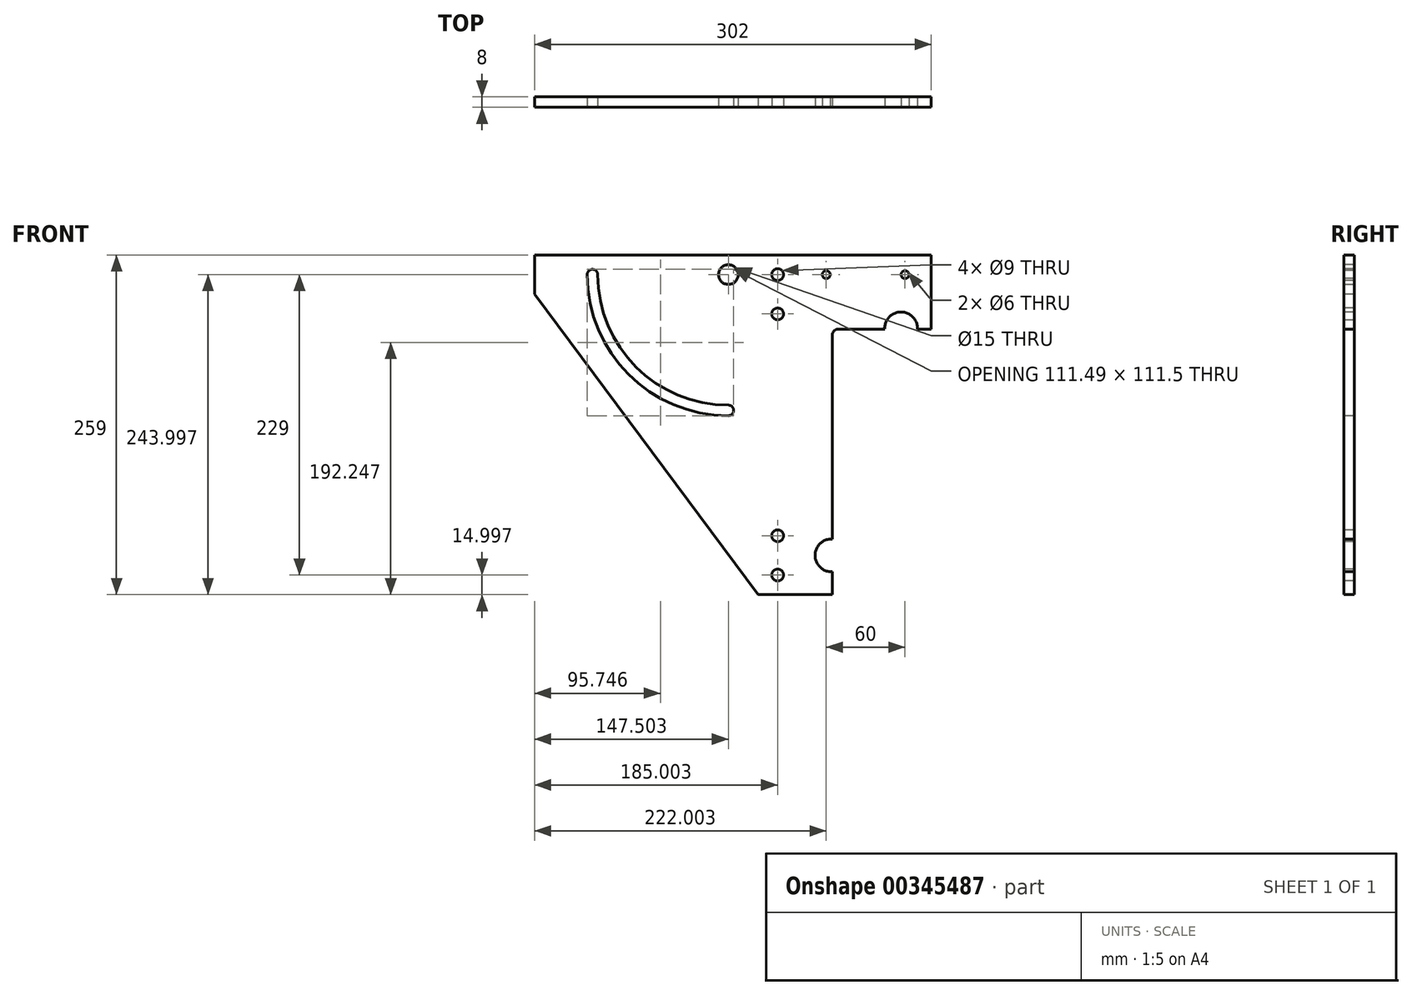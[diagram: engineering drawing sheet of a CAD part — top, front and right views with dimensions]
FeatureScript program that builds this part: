
annotation { "Feature Type Name" : "Feature", "Feature Type Description" : "" }
export const myFeature = defineFeature(function(context is Context, id is Id, definition is map)
    precondition{}
    {
        {
            var Q0;
            Q0=qCreatedBy(makeId("Front.planeOp"),FACE);
            var sketch = newSketch(context, id + "F0", { "sketchPlane" : qUnion([Q0])});
            skLineSegment(sketch, "E0.0.0", {"start": v(44.24, 117.76) * mm, "end": v(8.81, 117.76) * mm});
            skLineSegment(sketch, "E0.0.1", {"start": v(8.81, 117.76) * mm, "end": v(0.54, 111.96) * mm});
            skArc(sketch, "E0.0.2", {"start": v(0.54, 111.96) * mm, "mid": v(0.32, 111.71) * mm, "end": v(0.24, 111.4) * mm});
            skLineSegment(sketch, "E0.0.3", {"start": v(0.24, 111.4) * mm, "end": v(0.24, 96.05) * mm});
            skArc(sketch, "E0.0.4", {"start": v(0.24, 96.05) * mm, "mid": v(0.3, 95.78) * mm, "end": v(0.45, 95.55) * mm});
            skLineSegment(sketch, "E0.0.5", {"start": v(0.45, 95.55) * mm, "end": v(4.54, 91.46) * mm});
            skArc(sketch, "E0.0.6", {"start": v(4.54, 91.46) * mm, "mid": v(4.76, 91.31) * mm, "end": v(5.03, 91.26) * mm});
            skLineSegment(sketch, "E0.0.7", {"start": v(5.03, 91.26) * mm, "end": v(11.74, 91.26) * mm});
            skArc(sketch, "E0.0.8", {"start": v(11.74, 91.26) * mm, "mid": v(12.1, 91.4) * mm, "end": v(12.24, 91.76) * mm});
            skArc(sketch, "E0.0.9", {"start": v(12.24, 91.76) * mm, "mid": v(27.6, 98.12) * mm, "end": v(21.24, 82.76) * mm});
            skArc(sketch, "E0.0.10", {"start": v(21.24, 82.76) * mm, "mid": v(20.89, 82.61) * mm, "end": v(20.74, 82.26) * mm});
            skLineSegment(sketch, "E0.0.11", {"start": v(20.74, 82.26) * mm, "end": v(20.74, 81.05) * mm});
            skArc(sketch, "E0.0.12", {"start": v(20.74, 81.05) * mm, "mid": v(20.8, 80.78) * mm, "end": v(20.95, 80.55) * mm});
            skLineSegment(sketch, "E0.0.13", {"start": v(20.95, 80.55) * mm, "end": v(22.04, 79.46) * mm});
            skArc(sketch, "E0.0.14", {"start": v(22.04, 79.46) * mm, "mid": v(22.26, 79.31) * mm, "end": v(22.53, 79.26) * mm});
            skLineSegment(sketch, "E0.0.15", {"start": v(22.53, 79.26) * mm, "end": v(31.95, 79.26) * mm});
            skArc(sketch, "E0.0.16", {"start": v(31.95, 79.26) * mm, "mid": v(32.22, 79.31) * mm, "end": v(32.45, 79.46) * mm});
            skLineSegment(sketch, "E0.0.17", {"start": v(32.45, 79.46) * mm, "end": v(44.04, 91.05) * mm});
            skArc(sketch, "E0.0.18", {"start": v(44.04, 91.05) * mm, "mid": v(44.19, 91.28) * mm, "end": v(44.24, 91.55) * mm});
            skLineSegment(sketch, "E0.0.19", {"start": v(44.24, 91.55) * mm, "end": v(44.24, 117.76) * mm});
            skLineSegment(sketch, "E1.0.0", {"start": v(-3.56, 77.96) * mm, "end": v(8.04, 77.96) * mm});
            skLineSegment(sketch, "E1.0.1", {"start": v(8.04, 77.96) * mm, "end": v(8.24, 77.76) * mm});
            skLineSegment(sketch, "E1.0.2", {"start": v(18.24, 77.76) * mm, "end": v(8.24, 77.76) * mm});
            skLineSegment(sketch, "E1.0.3", {"start": v(18.24, 77.76) * mm, "end": v(18.74, 77.76) * mm});
            skLineSegment(sketch, "E1.0.4", {"start": v(18.74, 77.76) * mm, "end": v(19.24, 78.26) * mm});
            skLineSegment(sketch, "E1.0.5", {"start": v(19.24, 78.26) * mm, "end": v(19.24, 82.27) * mm});
            skArc(sketch, "E1.0.6", {"start": v(19.24, 82.27) * mm, "mid": v(19.71, 83.36) * mm, "end": v(20.82, 83.77) * mm});
            skArc(sketch, "E1.0.7", {"start": v(20.82, 83.77) * mm, "mid": v(26.72, 97.6) * mm, "end": v(13.3, 90.83) * mm});
            skArc(sketch, "E1.0.8", {"start": v(13.3, 90.83) * mm, "mid": v(13.3, 90.56) * mm, "end": v(13.2, 90.3) * mm});
            skLineSegment(sketch, "E1.0.9", {"start": v(13.2, 90.3) * mm, "end": v(11.09, 85.74) * mm});
            skArc(sketch, "E1.0.10", {"start": v(11.09, 85.74) * mm, "mid": v(10.72, 85.39) * mm, "end": v(10.23, 85.26) * mm});
            skLineSegment(sketch, "E1.0.11", {"start": v(10.23, 85.26) * mm, "end": v(2.74, 85.26) * mm});
            skLineSegment(sketch, "E1.0.12", {"start": v(2.74, 85.26) * mm, "end": v(2.24, 84.97) * mm});
            skLineSegment(sketch, "E1.0.13", {"start": v(2.24, 84.97) * mm, "end": v(1.74, 85.26) * mm});
            skLineSegment(sketch, "E1.0.14", {"start": v(1.74, 85.26) * mm, "end": v(-7.36, 85.26) * mm});
            skLineSegment(sketch, "E1.0.15", {"start": v(-7.36, 85.26) * mm, "end": v(-7.76, 84.86) * mm});
            skLineSegment(sketch, "E1.0.16", {"start": v(-7.76, 84.86) * mm, "end": v(-7.76, 78.16) * mm});
            skLineSegment(sketch, "E1.0.17", {"start": v(-7.76, 78.16) * mm, "end": v(-7.36, 77.76) * mm});
            skLineSegment(sketch, "E1.0.18", {"start": v(-3.76, 77.76) * mm, "end": v(-7.36, 77.76) * mm});
            skLineSegment(sketch, "E1.0.19", {"start": v(-3.76, 77.76) * mm, "end": v(-3.56, 77.96) * mm});
            skArc(sketch, "E2.0.0", {"start": v(-13.76, -69.24) * mm, "mid": v(-13.4, -69.1) * mm, "end": v(-13.26, -68.74) * mm});
            skLineSegment(sketch, "E2.0.1", {"start": v(-13.26, -68.74) * mm, "end": v(-13.26, -67.24) * mm});
            skArc(sketch, "E2.0.2", {"start": v(-13.26, -67.24) * mm, "mid": v(-13.55, -66.54) * mm, "end": v(-14.26, -66.24) * mm});
            skLineSegment(sketch, "E2.0.3", {"start": v(-14.26, -66.24) * mm, "end": v(-16.26, -66.24) * mm});
            skArc(sketch, "E2.0.4", {"start": v(-16.26, -66.24) * mm, "mid": v(-17.32, -66.68) * mm, "end": v(-17.76, -67.74) * mm});
            skLineSegment(sketch, "E2.0.5", {"start": v(-17.76, -67.74) * mm, "end": v(-17.76, -68.24) * mm});
            skLineSegment(sketch, "E2.0.6", {"start": v(-17.76, -68.24) * mm, "end": v(-17.76, -78.24) * mm});
            skArc(sketch, "E2.0.7", {"start": v(-17.76, -78.24) * mm, "mid": v(-16.59, -81.07) * mm, "end": v(-13.76, -82.24) * mm});
            skLineSegment(sketch, "E2.0.8", {"start": v(-13.76, -82.24) * mm, "end": v(-3.26, -82.24) * mm});
            skArc(sketch, "E2.0.9", {"start": v(-3.26, -82.24) * mm, "mid": v(-2.2, -81.8) * mm, "end": v(-1.76, -80.74) * mm});
            skLineSegment(sketch, "E2.0.10", {"start": v(-1.76, -80.74) * mm, "end": v(-1.76, -78.74) * mm});
            skArc(sketch, "E2.0.11", {"start": v(-1.76, -78.74) * mm, "mid": v(-2.05, -78.04) * mm, "end": v(-2.76, -77.74) * mm});
            skLineSegment(sketch, "E2.0.12", {"start": v(-2.76, -77.74) * mm, "end": v(-4.26, -77.74) * mm});
            skArc(sketch, "E2.0.13", {"start": v(-4.26, -77.74) * mm, "mid": v(-4.61, -77.89) * mm, "end": v(-4.76, -78.24) * mm});
            skLineSegment(sketch, "E2.0.14", {"start": v(-4.76, -78.24) * mm, "end": v(-4.76, -79.8) * mm});
            skArc(sketch, "E2.0.15", {"start": v(-4.76, -79.8) * mm, "mid": v(-4.89, -80.11) * mm, "end": v(-5.2, -80.24) * mm});
            skLineSegment(sketch, "E2.0.16", {"start": v(-5.2, -80.24) * mm, "end": v(-5.26, -80.24) * mm});
            skArc(sketch, "E2.0.17", {"start": v(-5.26, -80.24) * mm, "mid": v(-7.03, -79.51) * mm, "end": v(-7.76, -77.74) * mm});
            skLineSegment(sketch, "E2.0.18", {"start": v(-7.76, -77.74) * mm, "end": v(-7.76, -76.44) * mm});
            skArc(sketch, "E2.0.19", {"start": v(-7.76, -76.44) * mm, "mid": v(-7.38, -74.52) * mm, "end": v(-6.3, -72.9) * mm});
            skLineSegment(sketch, "E2.0.20", {"start": v(-6.3, -72.9) * mm, "end": v(-4.85, -71.46) * mm});
            skArc(sketch, "E2.0.21", {"start": v(-4.85, -71.46) * mm, "mid": v(-3.23, -70.37) * mm, "end": v(-1.31, -70) * mm});
            skLineSegment(sketch, "E2.0.22", {"start": v(-1.31, -70) * mm, "end": v(5.8, -70) * mm});
            skArc(sketch, "E2.0.23", {"start": v(5.8, -70) * mm, "mid": v(7.71, -70.37) * mm, "end": v(9.34, -71.46) * mm});
            skLineSegment(sketch, "E2.0.24", {"start": v(9.34, -71.46) * mm, "end": v(10.78, -72.9) * mm});
            skArc(sketch, "E2.0.25", {"start": v(10.78, -72.9) * mm, "mid": v(11.86, -74.52) * mm, "end": v(12.24, -76.44) * mm});
            skLineSegment(sketch, "E2.0.26", {"start": v(12.24, -76.44) * mm, "end": v(12.24, -77.74) * mm});
            skArc(sketch, "E2.0.27", {"start": v(12.24, -77.74) * mm, "mid": v(11.51, -79.51) * mm, "end": v(9.74, -80.24) * mm});
            skLineSegment(sketch, "E2.0.28", {"start": v(9.74, -80.24) * mm, "end": v(9.7, -80.24) * mm});
            skArc(sketch, "E2.0.29", {"start": v(9.7, -80.24) * mm, "mid": v(9.37, -80.11) * mm, "end": v(9.24, -79.8) * mm});
            skLineSegment(sketch, "E2.0.30", {"start": v(9.24, -79.8) * mm, "end": v(9.24, -78.24) * mm});
            skArc(sketch, "E2.0.31", {"start": v(9.24, -78.24) * mm, "mid": v(9.1, -77.89) * mm, "end": v(8.74, -77.74) * mm});
            skLineSegment(sketch, "E2.0.32", {"start": v(8.74, -77.74) * mm, "end": v(7.24, -77.74) * mm});
            skArc(sketch, "E2.0.33", {"start": v(7.24, -77.74) * mm, "mid": v(6.54, -78.04) * mm, "end": v(6.24, -78.74) * mm});
            skLineSegment(sketch, "E2.0.34", {"start": v(6.24, -78.74) * mm, "end": v(6.24, -80.74) * mm});
            skArc(sketch, "E2.0.35", {"start": v(6.24, -80.74) * mm, "mid": v(6.68, -81.8) * mm, "end": v(7.74, -82.24) * mm});
            skLineSegment(sketch, "E2.0.36", {"start": v(7.74, -82.24) * mm, "end": v(18.24, -82.24) * mm});
            skArc(sketch, "E2.0.37", {"start": v(18.24, -82.24) * mm, "mid": v(21.07, -81.07) * mm, "end": v(22.24, -78.24) * mm});
            skLineSegment(sketch, "E2.0.38", {"start": v(22.24, -78.24) * mm, "end": v(22.24, -67.74) * mm});
            skArc(sketch, "E2.0.39", {"start": v(22.24, -67.74) * mm, "mid": v(21.8, -66.68) * mm, "end": v(20.74, -66.24) * mm});
            skLineSegment(sketch, "E2.0.40", {"start": v(20.74, -66.24) * mm, "end": v(18.74, -66.24) * mm});
            skArc(sketch, "E2.0.41", {"start": v(18.74, -66.24) * mm, "mid": v(18.04, -66.54) * mm, "end": v(17.74, -67.24) * mm});
            skLineSegment(sketch, "E2.0.42", {"start": v(17.74, -67.24) * mm, "end": v(17.74, -68.74) * mm});
            skArc(sketch, "E2.0.43", {"start": v(17.74, -68.74) * mm, "mid": v(17.89, -69.1) * mm, "end": v(18.24, -69.24) * mm});
            skLineSegment(sketch, "E2.0.44", {"start": v(18.24, -69.24) * mm, "end": v(19.8, -69.24) * mm});
            skArc(sketch, "E2.0.45", {"start": v(19.8, -69.24) * mm, "mid": v(20.11, -69.37) * mm, "end": v(20.24, -69.7) * mm});
            skLineSegment(sketch, "E2.0.46", {"start": v(20.24, -69.7) * mm, "end": v(20.24, -69.74) * mm});
            skArc(sketch, "E2.0.47", {"start": v(20.24, -69.74) * mm, "mid": v(19.51, -71.51) * mm, "end": v(17.74, -72.24) * mm});
            skLineSegment(sketch, "E2.0.48", {"start": v(17.74, -72.24) * mm, "end": v(16.44, -72.24) * mm});
            skArc(sketch, "E2.0.49", {"start": v(16.44, -72.24) * mm, "mid": v(14.52, -71.86) * mm, "end": v(12.9, -70.78) * mm});
            skLineSegment(sketch, "E2.0.50", {"start": v(12.9, -70.78) * mm, "end": v(11.46, -69.34) * mm});
            skArc(sketch, "E2.0.51", {"start": v(11.46, -69.34) * mm, "mid": v(10.37, -67.71) * mm, "end": v(10, -65.8) * mm});
            skLineSegment(sketch, "E2.0.52", {"start": v(10, -65.8) * mm, "end": v(10, -58.69) * mm});
            skArc(sketch, "E2.0.53", {"start": v(10, -58.69) * mm, "mid": v(10.37, -56.77) * mm, "end": v(11.46, -55.15) * mm});
            skLineSegment(sketch, "E2.0.54", {"start": v(11.46, -55.15) * mm, "end": v(12.9, -53.7) * mm});
            skArc(sketch, "E2.0.55", {"start": v(12.9, -53.7) * mm, "mid": v(14.52, -52.62) * mm, "end": v(16.44, -52.24) * mm});
            skLineSegment(sketch, "E2.0.56", {"start": v(16.44, -52.24) * mm, "end": v(17.74, -52.24) * mm});
            skArc(sketch, "E2.0.57", {"start": v(17.74, -52.24) * mm, "mid": v(19.51, -52.97) * mm, "end": v(20.24, -54.74) * mm});
            skLineSegment(sketch, "E2.0.58", {"start": v(20.24, -54.74) * mm, "end": v(20.24, -54.8) * mm});
            skArc(sketch, "E2.0.59", {"start": v(20.24, -54.8) * mm, "mid": v(20.11, -55.11) * mm, "end": v(19.8, -55.24) * mm});
            skLineSegment(sketch, "E2.0.60", {"start": v(19.8, -55.24) * mm, "end": v(18.24, -55.24) * mm});
            skArc(sketch, "E2.0.61", {"start": v(18.24, -55.24) * mm, "mid": v(17.89, -55.39) * mm, "end": v(17.74, -55.74) * mm});
            skLineSegment(sketch, "E2.0.62", {"start": v(17.74, -55.74) * mm, "end": v(17.74, -57.24) * mm});
            skArc(sketch, "E2.0.63", {"start": v(17.74, -57.24) * mm, "mid": v(18.04, -57.95) * mm, "end": v(18.74, -58.24) * mm});
            skLineSegment(sketch, "E2.0.64", {"start": v(18.74, -58.24) * mm, "end": v(20.74, -58.24) * mm});
            skArc(sketch, "E2.0.65", {"start": v(20.74, -58.24) * mm, "mid": v(21.8, -57.8) * mm, "end": v(22.24, -56.74) * mm});
            skLineSegment(sketch, "E2.0.66", {"start": v(22.24, -56.74) * mm, "end": v(22.24, -27.74) * mm});
            skArc(sketch, "E2.0.67", {"start": v(22.24, -27.74) * mm, "mid": v(21.8, -26.68) * mm, "end": v(20.74, -26.24) * mm});
            skLineSegment(sketch, "E2.0.68", {"start": v(20.74, -26.24) * mm, "end": v(18.74, -26.24) * mm});
            skArc(sketch, "E2.0.69", {"start": v(18.74, -26.24) * mm, "mid": v(18.04, -26.54) * mm, "end": v(17.74, -27.24) * mm});
            skLineSegment(sketch, "E2.0.70", {"start": v(17.74, -27.24) * mm, "end": v(17.74, -28.74) * mm});
            skArc(sketch, "E2.0.71", {"start": v(17.74, -28.74) * mm, "mid": v(17.89, -29.1) * mm, "end": v(18.24, -29.24) * mm});
            skLineSegment(sketch, "E2.0.72", {"start": v(18.24, -29.24) * mm, "end": v(19.8, -29.24) * mm});
            skArc(sketch, "E2.0.73", {"start": v(19.8, -29.24) * mm, "mid": v(20.11, -29.37) * mm, "end": v(20.24, -29.7) * mm});
            skLineSegment(sketch, "E2.0.74", {"start": v(20.24, -29.7) * mm, "end": v(20.24, -29.74) * mm});
            skArc(sketch, "E2.0.75", {"start": v(20.24, -29.74) * mm, "mid": v(19.51, -31.51) * mm, "end": v(17.74, -32.24) * mm});
            skLineSegment(sketch, "E2.0.76", {"start": v(17.74, -32.24) * mm, "end": v(16.44, -32.24) * mm});
            skArc(sketch, "E2.0.77", {"start": v(16.44, -32.24) * mm, "mid": v(14.52, -31.86) * mm, "end": v(12.9, -30.78) * mm});
            skLineSegment(sketch, "E2.0.78", {"start": v(12.9, -30.78) * mm, "end": v(11.46, -29.34) * mm});
            skArc(sketch, "E2.0.79", {"start": v(11.46, -29.34) * mm, "mid": v(10.37, -27.71) * mm, "end": v(10, -25.8) * mm});
            skLineSegment(sketch, "E2.0.80", {"start": v(10, -25.8) * mm, "end": v(10, -18.69) * mm});
            skArc(sketch, "E2.0.81", {"start": v(10, -18.69) * mm, "mid": v(10.37, -16.77) * mm, "end": v(11.46, -15.15) * mm});
            skLineSegment(sketch, "E2.0.82", {"start": v(11.46, -15.15) * mm, "end": v(12.9, -13.7) * mm});
            skArc(sketch, "E2.0.83", {"start": v(12.9, -13.7) * mm, "mid": v(14.52, -12.62) * mm, "end": v(16.44, -12.24) * mm});
            skLineSegment(sketch, "E2.0.84", {"start": v(16.44, -12.24) * mm, "end": v(17.74, -12.24) * mm});
            skArc(sketch, "E2.0.85", {"start": v(17.74, -12.24) * mm, "mid": v(19.51, -12.97) * mm, "end": v(20.24, -14.74) * mm});
            skLineSegment(sketch, "E2.0.86", {"start": v(20.24, -14.74) * mm, "end": v(20.24, -14.8) * mm});
            skArc(sketch, "E2.0.87", {"start": v(20.24, -14.8) * mm, "mid": v(20.11, -15.11) * mm, "end": v(19.8, -15.24) * mm});
            skLineSegment(sketch, "E2.0.88", {"start": v(19.8, -15.24) * mm, "end": v(18.24, -15.24) * mm});
            skArc(sketch, "E2.0.89", {"start": v(18.24, -15.24) * mm, "mid": v(17.89, -15.39) * mm, "end": v(17.74, -15.74) * mm});
            skLineSegment(sketch, "E2.0.90", {"start": v(17.74, -15.74) * mm, "end": v(17.74, -17.24) * mm});
            skArc(sketch, "E2.0.91", {"start": v(17.74, -17.24) * mm, "mid": v(18.04, -17.95) * mm, "end": v(18.74, -18.24) * mm});
            skLineSegment(sketch, "E2.0.92", {"start": v(18.74, -18.24) * mm, "end": v(20.74, -18.24) * mm});
            skArc(sketch, "E2.0.93", {"start": v(20.74, -18.24) * mm, "mid": v(21.8, -17.8) * mm, "end": v(22.24, -16.74) * mm});
            skLineSegment(sketch, "E2.0.94", {"start": v(22.24, -16.74) * mm, "end": v(22.24, 12.26) * mm});
            skArc(sketch, "E2.0.95", {"start": v(22.24, 12.26) * mm, "mid": v(21.8, 13.32) * mm, "end": v(20.74, 13.76) * mm});
            skLineSegment(sketch, "E2.0.96", {"start": v(20.74, 13.76) * mm, "end": v(18.74, 13.76) * mm});
            skArc(sketch, "E2.0.97", {"start": v(18.74, 13.76) * mm, "mid": v(18.04, 13.46) * mm, "end": v(17.74, 12.76) * mm});
            skLineSegment(sketch, "E2.0.98", {"start": v(17.74, 12.76) * mm, "end": v(17.74, 11.26) * mm});
            skArc(sketch, "E2.0.99", {"start": v(17.74, 11.26) * mm, "mid": v(17.89, 10.9) * mm, "end": v(18.24, 10.76) * mm});
            skLineSegment(sketch, "E2.0.100", {"start": v(18.24, 10.76) * mm, "end": v(19.8, 10.76) * mm});
            skArc(sketch, "E2.0.101", {"start": v(19.8, 10.76) * mm, "mid": v(20.11, 10.63) * mm, "end": v(20.24, 10.3) * mm});
            skLineSegment(sketch, "E2.0.102", {"start": v(20.24, 10.3) * mm, "end": v(20.24, 10.26) * mm});
            skArc(sketch, "E2.0.103", {"start": v(20.24, 10.26) * mm, "mid": v(19.51, 8.49) * mm, "end": v(17.74, 7.76) * mm});
            skLineSegment(sketch, "E2.0.104", {"start": v(17.74, 7.76) * mm, "end": v(16.44, 7.76) * mm});
            skArc(sketch, "E2.0.105", {"start": v(16.44, 7.76) * mm, "mid": v(14.52, 8.14) * mm, "end": v(12.9, 9.22) * mm});
            skLineSegment(sketch, "E2.0.106", {"start": v(12.9, 9.22) * mm, "end": v(11.46, 10.66) * mm});
            skArc(sketch, "E2.0.107", {"start": v(11.46, 10.66) * mm, "mid": v(10.37, 12.29) * mm, "end": v(10, 14.2) * mm});
            skLineSegment(sketch, "E2.0.108", {"start": v(10, 14.2) * mm, "end": v(10, 21.31) * mm});
            skArc(sketch, "E2.0.109", {"start": v(10, 21.31) * mm, "mid": v(10.37, 23.23) * mm, "end": v(11.46, 24.85) * mm});
            skLineSegment(sketch, "E2.0.110", {"start": v(11.46, 24.85) * mm, "end": v(12.9, 26.3) * mm});
            skArc(sketch, "E2.0.111", {"start": v(12.9, 26.3) * mm, "mid": v(14.52, 27.38) * mm, "end": v(16.44, 27.76) * mm});
            skLineSegment(sketch, "E2.0.112", {"start": v(16.44, 27.76) * mm, "end": v(17.74, 27.76) * mm});
            skArc(sketch, "E2.0.113", {"start": v(17.74, 27.76) * mm, "mid": v(19.51, 27.03) * mm, "end": v(20.24, 25.26) * mm});
            skLineSegment(sketch, "E2.0.114", {"start": v(20.24, 25.26) * mm, "end": v(20.24, 25.2) * mm});
            skArc(sketch, "E2.0.115", {"start": v(20.24, 25.2) * mm, "mid": v(20.11, 24.89) * mm, "end": v(19.8, 24.76) * mm});
            skLineSegment(sketch, "E2.0.116", {"start": v(19.8, 24.76) * mm, "end": v(18.24, 24.76) * mm});
            skArc(sketch, "E2.0.117", {"start": v(18.24, 24.76) * mm, "mid": v(17.89, 24.61) * mm, "end": v(17.74, 24.26) * mm});
            skLineSegment(sketch, "E2.0.118", {"start": v(17.74, 24.26) * mm, "end": v(17.74, 22.76) * mm});
            skArc(sketch, "E2.0.119", {"start": v(17.74, 22.76) * mm, "mid": v(18.04, 22.05) * mm, "end": v(18.74, 21.76) * mm});
            skLineSegment(sketch, "E2.0.120", {"start": v(18.74, 21.76) * mm, "end": v(20.74, 21.76) * mm});
            skArc(sketch, "E2.0.121", {"start": v(20.74, 21.76) * mm, "mid": v(21.8, 22.2) * mm, "end": v(22.24, 23.26) * mm});
            skLineSegment(sketch, "E2.0.122", {"start": v(22.24, 23.26) * mm, "end": v(22.24, 52.26) * mm});
            skArc(sketch, "E2.0.123", {"start": v(22.24, 52.26) * mm, "mid": v(21.8, 53.32) * mm, "end": v(20.74, 53.76) * mm});
            skLineSegment(sketch, "E2.0.124", {"start": v(20.74, 53.76) * mm, "end": v(18.74, 53.76) * mm});
            skArc(sketch, "E2.0.125", {"start": v(18.74, 53.76) * mm, "mid": v(18.04, 53.46) * mm, "end": v(17.74, 52.76) * mm});
            skLineSegment(sketch, "E2.0.126", {"start": v(17.74, 52.76) * mm, "end": v(17.74, 51.26) * mm});
            skArc(sketch, "E2.0.127", {"start": v(17.74, 51.26) * mm, "mid": v(17.89, 50.9) * mm, "end": v(18.24, 50.76) * mm});
            skLineSegment(sketch, "E2.0.128", {"start": v(18.24, 50.76) * mm, "end": v(19.8, 50.76) * mm});
            skArc(sketch, "E2.0.129", {"start": v(19.8, 50.76) * mm, "mid": v(20.11, 50.63) * mm, "end": v(20.24, 50.3) * mm});
            skLineSegment(sketch, "E2.0.130", {"start": v(20.24, 50.3) * mm, "end": v(20.24, 50.26) * mm});
            skArc(sketch, "E2.0.131", {"start": v(20.24, 50.26) * mm, "mid": v(19.51, 48.49) * mm, "end": v(17.74, 47.76) * mm});
            skLineSegment(sketch, "E2.0.132", {"start": v(17.74, 47.76) * mm, "end": v(16.44, 47.76) * mm});
            skArc(sketch, "E2.0.133", {"start": v(16.44, 47.76) * mm, "mid": v(14.52, 48.14) * mm, "end": v(12.9, 49.22) * mm});
            skLineSegment(sketch, "E2.0.134", {"start": v(12.9, 49.22) * mm, "end": v(11.46, 50.66) * mm});
            skArc(sketch, "E2.0.135", {"start": v(11.46, 50.66) * mm, "mid": v(10.37, 52.29) * mm, "end": v(10, 54.2) * mm});
            skLineSegment(sketch, "E2.0.136", {"start": v(10, 54.2) * mm, "end": v(10, 61.31) * mm});
            skArc(sketch, "E2.0.137", {"start": v(10, 61.31) * mm, "mid": v(10.37, 63.23) * mm, "end": v(11.46, 64.85) * mm});
            skLineSegment(sketch, "E2.0.138", {"start": v(11.46, 64.85) * mm, "end": v(12.9, 66.3) * mm});
            skArc(sketch, "E2.0.139", {"start": v(12.9, 66.3) * mm, "mid": v(14.52, 67.38) * mm, "end": v(16.44, 67.76) * mm});
            skLineSegment(sketch, "E2.0.140", {"start": v(16.44, 67.76) * mm, "end": v(17.74, 67.76) * mm});
            skArc(sketch, "E2.0.141", {"start": v(17.74, 67.76) * mm, "mid": v(19.51, 67.03) * mm, "end": v(20.24, 65.26) * mm});
            skLineSegment(sketch, "E2.0.142", {"start": v(20.24, 65.26) * mm, "end": v(20.24, 65.2) * mm});
            skArc(sketch, "E2.0.143", {"start": v(20.24, 65.2) * mm, "mid": v(20.11, 64.89) * mm, "end": v(19.8, 64.76) * mm});
            skLineSegment(sketch, "E2.0.144", {"start": v(19.8, 64.76) * mm, "end": v(18.24, 64.76) * mm});
            skArc(sketch, "E2.0.145", {"start": v(18.24, 64.76) * mm, "mid": v(17.89, 64.61) * mm, "end": v(17.74, 64.26) * mm});
            skLineSegment(sketch, "E2.0.146", {"start": v(17.74, 64.26) * mm, "end": v(17.74, 62.76) * mm});
            skArc(sketch, "E2.0.147", {"start": v(17.74, 62.76) * mm, "mid": v(18.04, 62.05) * mm, "end": v(18.74, 61.76) * mm});
            skLineSegment(sketch, "E2.0.148", {"start": v(18.74, 61.76) * mm, "end": v(20.74, 61.76) * mm});
            skArc(sketch, "E2.0.149", {"start": v(20.74, 61.76) * mm, "mid": v(21.8, 62.2) * mm, "end": v(22.24, 63.26) * mm});
            skLineSegment(sketch, "E2.0.150", {"start": v(22.24, 63.26) * mm, "end": v(22.24, 73.76) * mm});
            skArc(sketch, "E2.0.151", {"start": v(22.24, 73.76) * mm, "mid": v(21.07, 76.59) * mm, "end": v(18.24, 77.76) * mm});
            skLineSegment(sketch, "E2.0.153", {"start": v(8.24, 77.76) * mm, "end": v(7.74, 77.76) * mm});
            skArc(sketch, "E2.0.154", {"start": v(7.74, 77.76) * mm, "mid": v(6.68, 77.32) * mm, "end": v(6.24, 76.26) * mm});
            skLineSegment(sketch, "E2.0.155", {"start": v(6.24, 76.26) * mm, "end": v(6.24, 74.26) * mm});
            skArc(sketch, "E2.0.156", {"start": v(6.24, 74.26) * mm, "mid": v(6.54, 73.55) * mm, "end": v(7.24, 73.26) * mm});
            skLineSegment(sketch, "E2.0.157", {"start": v(7.24, 73.26) * mm, "end": v(8.74, 73.26) * mm});
            skArc(sketch, "E2.0.158", {"start": v(8.74, 73.26) * mm, "mid": v(9.1, 73.4) * mm, "end": v(9.24, 73.76) * mm});
            skLineSegment(sketch, "E2.0.159", {"start": v(9.24, 73.76) * mm, "end": v(9.24, 75.3) * mm});
            skArc(sketch, "E2.0.160", {"start": v(9.24, 75.3) * mm, "mid": v(9.37, 75.63) * mm, "end": v(9.7, 75.76) * mm});
            skLineSegment(sketch, "E2.0.161", {"start": v(9.7, 75.76) * mm, "end": v(9.74, 75.76) * mm});
            skArc(sketch, "E2.0.162", {"start": v(9.74, 75.76) * mm, "mid": v(11.51, 75.03) * mm, "end": v(12.24, 73.26) * mm});
            skLineSegment(sketch, "E2.0.163", {"start": v(12.24, 73.26) * mm, "end": v(12.24, 71.95) * mm});
            skArc(sketch, "E2.0.164", {"start": v(12.24, 71.95) * mm, "mid": v(11.86, 70.04) * mm, "end": v(10.78, 68.41) * mm});
            skLineSegment(sketch, "E2.0.165", {"start": v(10.78, 68.41) * mm, "end": v(9.34, 66.97) * mm});
            skArc(sketch, "E2.0.166", {"start": v(9.34, 66.97) * mm, "mid": v(7.71, 65.89) * mm, "end": v(5.8, 65.5) * mm});
            skLineSegment(sketch, "E2.0.167", {"start": v(5.8, 65.5) * mm, "end": v(-1.31, 65.5) * mm});
            skArc(sketch, "E2.0.168", {"start": v(-1.31, 65.5) * mm, "mid": v(-3.23, 65.89) * mm, "end": v(-4.85, 66.97) * mm});
            skLineSegment(sketch, "E2.0.169", {"start": v(-4.85, 66.97) * mm, "end": v(-6.3, 68.41) * mm});
            skArc(sketch, "E2.0.170", {"start": v(-6.3, 68.41) * mm, "mid": v(-7.38, 70.04) * mm, "end": v(-7.76, 71.95) * mm});
            skLineSegment(sketch, "E2.0.171", {"start": v(-7.76, 71.95) * mm, "end": v(-7.76, 73.26) * mm});
            skArc(sketch, "E2.0.172", {"start": v(-7.76, 73.26) * mm, "mid": v(-7.03, 75.03) * mm, "end": v(-5.26, 75.76) * mm});
            skLineSegment(sketch, "E2.0.173", {"start": v(-5.26, 75.76) * mm, "end": v(-5.2, 75.76) * mm});
            skArc(sketch, "E2.0.174", {"start": v(-5.2, 75.76) * mm, "mid": v(-4.89, 75.63) * mm, "end": v(-4.76, 75.3) * mm});
            skLineSegment(sketch, "E2.0.175", {"start": v(-4.76, 75.3) * mm, "end": v(-4.76, 73.76) * mm});
            skArc(sketch, "E2.0.176", {"start": v(-4.76, 73.76) * mm, "mid": v(-4.61, 73.4) * mm, "end": v(-4.26, 73.26) * mm});
            skLineSegment(sketch, "E2.0.177", {"start": v(-4.26, 73.26) * mm, "end": v(-2.76, 73.26) * mm});
            skArc(sketch, "E2.0.178", {"start": v(-2.76, 73.26) * mm, "mid": v(-2.05, 73.55) * mm, "end": v(-1.76, 74.26) * mm});
            skLineSegment(sketch, "E2.0.179", {"start": v(-1.76, 74.26) * mm, "end": v(-1.76, 76.26) * mm});
            skArc(sketch, "E2.0.180", {"start": v(-1.76, 76.26) * mm, "mid": v(-2.2, 77.32) * mm, "end": v(-3.26, 77.76) * mm});
            skLineSegment(sketch, "E2.0.181", {"start": v(-3.26, 77.76) * mm, "end": v(-3.76, 77.76) * mm});
            skLineSegment(sketch, "E2.0.183", {"start": v(-7.36, 77.76) * mm, "end": v(-13.76, 77.76) * mm});
            skArc(sketch, "E2.0.184", {"start": v(-13.76, 77.76) * mm, "mid": v(-16.59, 76.59) * mm, "end": v(-17.76, 73.76) * mm});
            skLineSegment(sketch, "E2.0.185", {"start": v(-17.76, 73.76) * mm, "end": v(-17.76, 63.26) * mm});
            skArc(sketch, "E2.0.186", {"start": v(-17.76, 63.26) * mm, "mid": v(-17.32, 62.2) * mm, "end": v(-16.26, 61.76) * mm});
            skLineSegment(sketch, "E2.0.187", {"start": v(-16.26, 61.76) * mm, "end": v(-14.26, 61.76) * mm});
            skArc(sketch, "E2.0.188", {"start": v(-14.26, 61.76) * mm, "mid": v(-13.55, 62.05) * mm, "end": v(-13.26, 62.76) * mm});
            skLineSegment(sketch, "E2.0.189", {"start": v(-13.26, 62.76) * mm, "end": v(-13.26, 64.26) * mm});
            skArc(sketch, "E2.0.190", {"start": v(-13.26, 64.26) * mm, "mid": v(-13.4, 64.61) * mm, "end": v(-13.76, 64.76) * mm});
            skLineSegment(sketch, "E2.0.191", {"start": v(-13.76, 64.76) * mm, "end": v(-15.3, 64.76) * mm});
            skArc(sketch, "E2.0.192", {"start": v(-15.3, 64.76) * mm, "mid": v(-15.63, 64.89) * mm, "end": v(-15.76, 65.2) * mm});
            skLineSegment(sketch, "E2.0.193", {"start": v(-15.76, 65.2) * mm, "end": v(-15.76, 65.26) * mm});
            skArc(sketch, "E2.0.194", {"start": v(-15.76, 65.26) * mm, "mid": v(-15.03, 67.03) * mm, "end": v(-13.26, 67.76) * mm});
            skLineSegment(sketch, "E2.0.195", {"start": v(-13.26, 67.76) * mm, "end": v(-11.95, 67.76) * mm});
            skArc(sketch, "E2.0.196", {"start": v(-11.95, 67.76) * mm, "mid": v(-10.04, 67.38) * mm, "end": v(-8.41, 66.3) * mm});
            skLineSegment(sketch, "E2.0.197", {"start": v(-8.41, 66.3) * mm, "end": v(-6.97, 64.85) * mm});
            skArc(sketch, "E2.0.198", {"start": v(-6.97, 64.85) * mm, "mid": v(-5.89, 63.23) * mm, "end": v(-5.5, 61.31) * mm});
            skLineSegment(sketch, "E2.0.199", {"start": v(-5.5, 61.31) * mm, "end": v(-5.5, 54.2) * mm});
            skArc(sketch, "E2.0.200", {"start": v(-5.5, 54.2) * mm, "mid": v(-5.89, 52.29) * mm, "end": v(-6.97, 50.66) * mm});
            skLineSegment(sketch, "E2.0.201", {"start": v(-6.97, 50.66) * mm, "end": v(-8.41, 49.22) * mm});
            skArc(sketch, "E2.0.202", {"start": v(-8.41, 49.22) * mm, "mid": v(-10.04, 48.14) * mm, "end": v(-11.95, 47.76) * mm});
            skLineSegment(sketch, "E2.0.203", {"start": v(-11.95, 47.76) * mm, "end": v(-13.26, 47.76) * mm});
            skArc(sketch, "E2.0.204", {"start": v(-13.26, 47.76) * mm, "mid": v(-15.03, 48.49) * mm, "end": v(-15.76, 50.26) * mm});
            skLineSegment(sketch, "E2.0.205", {"start": v(-15.76, 50.26) * mm, "end": v(-15.76, 50.3) * mm});
            skArc(sketch, "E2.0.206", {"start": v(-15.76, 50.3) * mm, "mid": v(-15.63, 50.63) * mm, "end": v(-15.3, 50.76) * mm});
            skLineSegment(sketch, "E2.0.207", {"start": v(-15.3, 50.76) * mm, "end": v(-13.76, 50.76) * mm});
            skArc(sketch, "E2.0.208", {"start": v(-13.76, 50.76) * mm, "mid": v(-13.4, 50.9) * mm, "end": v(-13.26, 51.26) * mm});
            skLineSegment(sketch, "E2.0.209", {"start": v(-13.26, 51.26) * mm, "end": v(-13.26, 52.76) * mm});
            skArc(sketch, "E2.0.210", {"start": v(-13.26, 52.76) * mm, "mid": v(-13.55, 53.46) * mm, "end": v(-14.26, 53.76) * mm});
            skLineSegment(sketch, "E2.0.211", {"start": v(-14.26, 53.76) * mm, "end": v(-16.26, 53.76) * mm});
            skArc(sketch, "E2.0.212", {"start": v(-16.26, 53.76) * mm, "mid": v(-17.32, 53.32) * mm, "end": v(-17.76, 52.26) * mm});
            skLineSegment(sketch, "E2.0.213", {"start": v(-17.76, 52.26) * mm, "end": v(-17.76, 23.26) * mm});
            skArc(sketch, "E2.0.214", {"start": v(-17.76, 23.26) * mm, "mid": v(-17.32, 22.2) * mm, "end": v(-16.26, 21.76) * mm});
            skLineSegment(sketch, "E2.0.215", {"start": v(-16.26, 21.76) * mm, "end": v(-14.26, 21.76) * mm});
            skArc(sketch, "E2.0.216", {"start": v(-14.26, 21.76) * mm, "mid": v(-13.55, 22.05) * mm, "end": v(-13.26, 22.76) * mm});
            skLineSegment(sketch, "E2.0.217", {"start": v(-13.26, 22.76) * mm, "end": v(-13.26, 24.26) * mm});
            skArc(sketch, "E2.0.218", {"start": v(-13.26, 24.26) * mm, "mid": v(-13.4, 24.61) * mm, "end": v(-13.76, 24.76) * mm});
            skLineSegment(sketch, "E2.0.219", {"start": v(-13.76, 24.76) * mm, "end": v(-15.3, 24.76) * mm});
            skArc(sketch, "E2.0.220", {"start": v(-15.3, 24.76) * mm, "mid": v(-15.63, 24.89) * mm, "end": v(-15.76, 25.2) * mm});
            skLineSegment(sketch, "E2.0.221", {"start": v(-15.76, 25.2) * mm, "end": v(-15.76, 25.26) * mm});
            skArc(sketch, "E2.0.222", {"start": v(-15.76, 25.26) * mm, "mid": v(-15.03, 27.03) * mm, "end": v(-13.26, 27.76) * mm});
            skLineSegment(sketch, "E2.0.223", {"start": v(-13.26, 27.76) * mm, "end": v(-11.95, 27.76) * mm});
            skArc(sketch, "E2.0.224", {"start": v(-11.95, 27.76) * mm, "mid": v(-10.04, 27.38) * mm, "end": v(-8.41, 26.3) * mm});
            skLineSegment(sketch, "E2.0.225", {"start": v(-8.41, 26.3) * mm, "end": v(-6.97, 24.85) * mm});
            skArc(sketch, "E2.0.226", {"start": v(-6.97, 24.85) * mm, "mid": v(-5.89, 23.23) * mm, "end": v(-5.5, 21.31) * mm});
            skLineSegment(sketch, "E2.0.227", {"start": v(-5.5, 21.31) * mm, "end": v(-5.5, 14.2) * mm});
            skArc(sketch, "E2.0.228", {"start": v(-5.5, 14.2) * mm, "mid": v(-5.89, 12.29) * mm, "end": v(-6.97, 10.66) * mm});
            skLineSegment(sketch, "E2.0.229", {"start": v(-6.97, 10.66) * mm, "end": v(-8.41, 9.22) * mm});
            skArc(sketch, "E2.0.230", {"start": v(-8.41, 9.22) * mm, "mid": v(-10.04, 8.14) * mm, "end": v(-11.95, 7.76) * mm});
            skLineSegment(sketch, "E2.0.231", {"start": v(-11.95, 7.76) * mm, "end": v(-13.26, 7.76) * mm});
            skArc(sketch, "E2.0.232", {"start": v(-13.26, 7.76) * mm, "mid": v(-15.03, 8.49) * mm, "end": v(-15.76, 10.26) * mm});
            skLineSegment(sketch, "E2.0.233", {"start": v(-15.76, 10.26) * mm, "end": v(-15.76, 10.3) * mm});
            skArc(sketch, "E2.0.234", {"start": v(-15.76, 10.3) * mm, "mid": v(-15.63, 10.63) * mm, "end": v(-15.3, 10.76) * mm});
            skLineSegment(sketch, "E2.0.235", {"start": v(-15.3, 10.76) * mm, "end": v(-13.76, 10.76) * mm});
            skArc(sketch, "E2.0.236", {"start": v(-13.76, 10.76) * mm, "mid": v(-13.4, 10.9) * mm, "end": v(-13.26, 11.26) * mm});
            skLineSegment(sketch, "E2.0.237", {"start": v(-13.26, 11.26) * mm, "end": v(-13.26, 12.76) * mm});
            skArc(sketch, "E2.0.238", {"start": v(-13.26, 12.76) * mm, "mid": v(-13.55, 13.46) * mm, "end": v(-14.26, 13.76) * mm});
            skLineSegment(sketch, "E2.0.239", {"start": v(-14.26, 13.76) * mm, "end": v(-16.26, 13.76) * mm});
            skArc(sketch, "E2.0.240", {"start": v(-16.26, 13.76) * mm, "mid": v(-17.32, 13.32) * mm, "end": v(-17.76, 12.26) * mm});
            skLineSegment(sketch, "E2.0.241", {"start": v(-17.76, 12.26) * mm, "end": v(-17.76, -16.74) * mm});
            skArc(sketch, "E2.0.242", {"start": v(-17.76, -16.74) * mm, "mid": v(-17.32, -17.8) * mm, "end": v(-16.26, -18.24) * mm});
            skLineSegment(sketch, "E2.0.243", {"start": v(-16.26, -18.24) * mm, "end": v(-14.26, -18.24) * mm});
            skArc(sketch, "E2.0.244", {"start": v(-14.26, -18.24) * mm, "mid": v(-13.55, -17.95) * mm, "end": v(-13.26, -17.24) * mm});
            skLineSegment(sketch, "E2.0.245", {"start": v(-13.26, -17.24) * mm, "end": v(-13.26, -15.74) * mm});
            skArc(sketch, "E2.0.246", {"start": v(-13.26, -15.74) * mm, "mid": v(-13.4, -15.39) * mm, "end": v(-13.76, -15.24) * mm});
            skLineSegment(sketch, "E2.0.247", {"start": v(-13.76, -15.24) * mm, "end": v(-15.3, -15.24) * mm});
            skArc(sketch, "E2.0.248", {"start": v(-15.3, -15.24) * mm, "mid": v(-15.63, -15.11) * mm, "end": v(-15.76, -14.8) * mm});
            skLineSegment(sketch, "E2.0.249", {"start": v(-15.76, -14.8) * mm, "end": v(-15.76, -14.74) * mm});
            skArc(sketch, "E2.0.250", {"start": v(-15.76, -14.74) * mm, "mid": v(-15.03, -12.97) * mm, "end": v(-13.26, -12.24) * mm});
            skLineSegment(sketch, "E2.0.251", {"start": v(-13.26, -12.24) * mm, "end": v(-11.95, -12.24) * mm});
            skArc(sketch, "E2.0.252", {"start": v(-11.95, -12.24) * mm, "mid": v(-10.04, -12.62) * mm, "end": v(-8.41, -13.7) * mm});
            skLineSegment(sketch, "E2.0.253", {"start": v(-8.41, -13.7) * mm, "end": v(-6.97, -15.15) * mm});
            skArc(sketch, "E2.0.254", {"start": v(-6.97, -15.15) * mm, "mid": v(-5.89, -16.77) * mm, "end": v(-5.5, -18.69) * mm});
            skLineSegment(sketch, "E2.0.255", {"start": v(-5.5, -18.69) * mm, "end": v(-5.5, -25.8) * mm});
            skArc(sketch, "E2.0.256", {"start": v(-5.5, -25.8) * mm, "mid": v(-5.89, -27.71) * mm, "end": v(-6.97, -29.34) * mm});
            skLineSegment(sketch, "E2.0.257", {"start": v(-6.97, -29.34) * mm, "end": v(-8.41, -30.78) * mm});
            skArc(sketch, "E2.0.258", {"start": v(-8.41, -30.78) * mm, "mid": v(-10.04, -31.86) * mm, "end": v(-11.95, -32.24) * mm});
            skLineSegment(sketch, "E2.0.259", {"start": v(-11.95, -32.24) * mm, "end": v(-13.26, -32.24) * mm});
            skArc(sketch, "E2.0.260", {"start": v(-13.26, -32.24) * mm, "mid": v(-15.03, -31.51) * mm, "end": v(-15.76, -29.74) * mm});
            skLineSegment(sketch, "E2.0.261", {"start": v(-15.76, -29.74) * mm, "end": v(-15.76, -29.7) * mm});
            skArc(sketch, "E2.0.262", {"start": v(-15.76, -29.7) * mm, "mid": v(-15.63, -29.37) * mm, "end": v(-15.3, -29.24) * mm});
            skLineSegment(sketch, "E2.0.263", {"start": v(-15.3, -29.24) * mm, "end": v(-13.76, -29.24) * mm});
            skArc(sketch, "E2.0.264", {"start": v(-13.76, -29.24) * mm, "mid": v(-13.4, -29.1) * mm, "end": v(-13.26, -28.74) * mm});
            skLineSegment(sketch, "E2.0.265", {"start": v(-13.26, -28.74) * mm, "end": v(-13.26, -27.24) * mm});
            skArc(sketch, "E2.0.266", {"start": v(-13.26, -27.24) * mm, "mid": v(-13.55, -26.54) * mm, "end": v(-14.26, -26.24) * mm});
            skLineSegment(sketch, "E2.0.267", {"start": v(-14.26, -26.24) * mm, "end": v(-16.26, -26.24) * mm});
            skArc(sketch, "E2.0.268", {"start": v(-16.26, -26.24) * mm, "mid": v(-17.32, -26.68) * mm, "end": v(-17.76, -27.74) * mm});
            skLineSegment(sketch, "E2.0.269", {"start": v(-17.76, -27.74) * mm, "end": v(-17.76, -52.64) * mm});
            skLineSegment(sketch, "E2.0.270", {"start": v(-17.76, -52.64) * mm, "end": v(-17.76, -56.24) * mm});
            skLineSegment(sketch, "E2.0.271", {"start": v(-17.76, -56.24) * mm, "end": v(-17.76, -56.74) * mm});
            skArc(sketch, "E2.0.272", {"start": v(-17.76, -56.74) * mm, "mid": v(-17.32, -57.8) * mm, "end": v(-16.26, -58.24) * mm});
            skLineSegment(sketch, "E2.0.273", {"start": v(-16.26, -58.24) * mm, "end": v(-14.26, -58.24) * mm});
            skArc(sketch, "E2.0.274", {"start": v(-14.26, -58.24) * mm, "mid": v(-13.55, -57.95) * mm, "end": v(-13.26, -57.24) * mm});
            skLineSegment(sketch, "E2.0.275", {"start": v(-13.26, -57.24) * mm, "end": v(-13.26, -55.74) * mm});
            skArc(sketch, "E2.0.276", {"start": v(-13.26, -55.74) * mm, "mid": v(-13.4, -55.39) * mm, "end": v(-13.76, -55.24) * mm});
            skLineSegment(sketch, "E2.0.277", {"start": v(-13.76, -55.24) * mm, "end": v(-15.3, -55.24) * mm});
            skArc(sketch, "E2.0.278", {"start": v(-15.3, -55.24) * mm, "mid": v(-15.63, -55.11) * mm, "end": v(-15.76, -54.8) * mm});
            skLineSegment(sketch, "E2.0.279", {"start": v(-15.76, -54.8) * mm, "end": v(-15.76, -54.74) * mm});
            skArc(sketch, "E2.0.280", {"start": v(-15.76, -54.74) * mm, "mid": v(-15.03, -52.97) * mm, "end": v(-13.26, -52.24) * mm});
            skLineSegment(sketch, "E2.0.281", {"start": v(-13.26, -52.24) * mm, "end": v(-11.95, -52.24) * mm});
            skArc(sketch, "E2.0.282", {"start": v(-11.95, -52.24) * mm, "mid": v(-10.04, -52.62) * mm, "end": v(-8.41, -53.7) * mm});
            skLineSegment(sketch, "E2.0.283", {"start": v(-8.41, -53.7) * mm, "end": v(-6.97, -55.15) * mm});
            skArc(sketch, "E2.0.284", {"start": v(-6.97, -55.15) * mm, "mid": v(-5.89, -56.77) * mm, "end": v(-5.5, -58.69) * mm});
            skLineSegment(sketch, "E2.0.285", {"start": v(-5.5, -58.69) * mm, "end": v(-5.5, -65.8) * mm});
            skArc(sketch, "E2.0.286", {"start": v(-5.5, -65.8) * mm, "mid": v(-5.89, -67.71) * mm, "end": v(-6.97, -69.34) * mm});
            skLineSegment(sketch, "E2.0.287", {"start": v(-6.97, -69.34) * mm, "end": v(-8.41, -70.78) * mm});
            skArc(sketch, "E2.0.288", {"start": v(-8.41, -70.78) * mm, "mid": v(-10.04, -71.86) * mm, "end": v(-11.95, -72.24) * mm});
            skLineSegment(sketch, "E2.0.289", {"start": v(-11.95, -72.24) * mm, "end": v(-13.26, -72.24) * mm});
            skArc(sketch, "E2.0.290", {"start": v(-13.26, -72.24) * mm, "mid": v(-15.03, -71.51) * mm, "end": v(-15.76, -69.74) * mm});
            skLineSegment(sketch, "E2.0.291", {"start": v(-15.76, -69.74) * mm, "end": v(-15.76, -69.7) * mm});
            skArc(sketch, "E2.0.292", {"start": v(-15.76, -69.7) * mm, "mid": v(-15.63, -69.37) * mm, "end": v(-15.3, -69.24) * mm});
            skLineSegment(sketch, "E2.0.293", {"start": v(-15.3, -69.24) * mm, "end": v(-13.76, -69.24) * mm});
            skLineSegment(sketch, "E3.0.0", {"start": v(-17.96, -68.04) * mm, "end": v(-17.96, -56.44) * mm});
            skLineSegment(sketch, "E3.0.1", {"start": v(-17.96, -56.44) * mm, "end": v(-17.76, -56.24) * mm});
            skLineSegment(sketch, "E3.0.2", {"start": v(-17.76, -56.24) * mm, "end": v(-17.76, -52.64) * mm});
            skLineSegment(sketch, "E3.0.3", {"start": v(-17.76, -52.64) * mm, "end": v(-18.16, -52.24) * mm});
            skLineSegment(sketch, "E3.0.4", {"start": v(-18.16, -52.24) * mm, "end": v(-24.86, -52.24) * mm});
            skLineSegment(sketch, "E3.0.5", {"start": v(-24.86, -52.24) * mm, "end": v(-25.26, -52.64) * mm});
            skLineSegment(sketch, "E3.0.6", {"start": v(-25.26, -52.64) * mm, "end": v(-25.26, -61.74) * mm});
            skLineSegment(sketch, "E3.0.7", {"start": v(-25.26, -61.74) * mm, "end": v(-24.97, -62.24) * mm});
            skLineSegment(sketch, "E3.0.8", {"start": v(-24.97, -62.24) * mm, "end": v(-25.26, -62.74) * mm});
            skLineSegment(sketch, "E3.0.9", {"start": v(-25.26, -62.74) * mm, "end": v(-25.26, -70.23) * mm});
            skArc(sketch, "E3.0.10", {"start": v(-25.26, -70.23) * mm, "mid": v(-25.39, -70.72) * mm, "end": v(-25.74, -71.09) * mm});
            skLineSegment(sketch, "E3.0.11", {"start": v(-25.74, -71.09) * mm, "end": v(-30.3, -73.2) * mm});
            skArc(sketch, "E3.0.12", {"start": v(-30.3, -73.2) * mm, "mid": v(-30.56, -73.3) * mm, "end": v(-30.83, -73.3) * mm});
            skArc(sketch, "E3.0.13", {"start": v(-30.83, -73.3) * mm, "mid": v(-37.6, -86.72) * mm, "end": v(-23.77, -80.82) * mm});
            skArc(sketch, "E3.0.14", {"start": v(-23.77, -80.82) * mm, "mid": v(-23.36, -79.71) * mm, "end": v(-22.27, -79.24) * mm});
            skLineSegment(sketch, "E3.0.15", {"start": v(-22.27, -79.24) * mm, "end": v(-18.26, -79.24) * mm});
            skLineSegment(sketch, "E3.0.16", {"start": v(-18.26, -79.24) * mm, "end": v(-17.76, -78.74) * mm});
            skLineSegment(sketch, "E3.0.17", {"start": v(-17.76, -78.74) * mm, "end": v(-17.76, -78.24) * mm});
            skLineSegment(sketch, "E3.0.18", {"start": v(-17.76, -78.24) * mm, "end": v(-17.76, -68.24) * mm});
            skLineSegment(sketch, "E3.0.19", {"start": v(-17.76, -68.24) * mm, "end": v(-17.96, -68.04) * mm});
            skLineSegment(sketch, "E4.0.0", {"start": v(-57.76, -68.81) * mm, "end": v(-57.76, -104.24) * mm});
            skLineSegment(sketch, "E4.0.1", {"start": v(-57.76, -104.24) * mm, "end": v(-31.55, -104.24) * mm});
            skArc(sketch, "E4.0.2", {"start": v(-31.55, -104.24) * mm, "mid": v(-31.28, -104.19) * mm, "end": v(-31.05, -104.04) * mm});
            skLineSegment(sketch, "E4.0.3", {"start": v(-31.05, -104.04) * mm, "end": v(-19.46, -92.45) * mm});
            skArc(sketch, "E4.0.4", {"start": v(-19.46, -92.45) * mm, "mid": v(-19.31, -92.22) * mm, "end": v(-19.26, -91.95) * mm});
            skLineSegment(sketch, "E4.0.5", {"start": v(-19.26, -91.95) * mm, "end": v(-19.26, -82.53) * mm});
            skArc(sketch, "E4.0.6", {"start": v(-19.26, -82.53) * mm, "mid": v(-19.31, -82.26) * mm, "end": v(-19.46, -82.04) * mm});
            skLineSegment(sketch, "E4.0.7", {"start": v(-19.46, -82.04) * mm, "end": v(-20.55, -80.95) * mm});
            skArc(sketch, "E4.0.8", {"start": v(-20.55, -80.95) * mm, "mid": v(-20.78, -80.8) * mm, "end": v(-21.05, -80.74) * mm});
            skLineSegment(sketch, "E4.0.9", {"start": v(-21.05, -80.74) * mm, "end": v(-22.26, -80.74) * mm});
            skArc(sketch, "E4.0.10", {"start": v(-22.26, -80.74) * mm, "mid": v(-22.61, -80.89) * mm, "end": v(-22.76, -81.24) * mm});
            skArc(sketch, "E4.0.11", {"start": v(-22.76, -81.24) * mm, "mid": v(-38.12, -87.6) * mm, "end": v(-31.76, -72.24) * mm});
            skArc(sketch, "E4.0.12", {"start": v(-31.76, -72.24) * mm, "mid": v(-31.4, -72.1) * mm, "end": v(-31.26, -71.74) * mm});
            skLineSegment(sketch, "E4.0.13", {"start": v(-31.26, -71.74) * mm, "end": v(-31.26, -65.03) * mm});
            skArc(sketch, "E4.0.14", {"start": v(-31.26, -65.03) * mm, "mid": v(-31.31, -64.76) * mm, "end": v(-31.46, -64.54) * mm});
            skLineSegment(sketch, "E4.0.15", {"start": v(-31.46, -64.54) * mm, "end": v(-35.55, -60.45) * mm});
            skArc(sketch, "E4.0.16", {"start": v(-35.55, -60.45) * mm, "mid": v(-35.78, -60.3) * mm, "end": v(-36.05, -60.24) * mm});
            skLineSegment(sketch, "E4.0.17", {"start": v(-36.05, -60.24) * mm, "end": v(-51.4, -60.24) * mm});
            skArc(sketch, "E4.0.18", {"start": v(-51.4, -60.24) * mm, "mid": v(-51.71, -60.32) * mm, "end": v(-51.96, -60.54) * mm});
            skLineSegment(sketch, "E4.0.19", {"start": v(-51.96, -60.54) * mm, "end": v(-57.76, -68.81) * mm});
            skSolve(sketch);
        }
        {
            var Q0;
            Q0=qCreatedBy(makeId("Front.planeOp"),FACE);
            var sketch = newSketch(context, id + "F1", { "sketchPlane" : qUnion([Q0])});
            skPoint(sketch, "E5.0", {"position": v(-57.76, -104.24) * mm});
            skPoint(sketch, "E6.0", {"position": v(-57.76, -68.81) * mm});
            skPoint(sketch, "E7.0", {"position": v(44.24, 117.76) * mm});
            skLineSegment(sketch, "E8", {"start": v(-257.76, 117.76) * mm, "end": v(-257.76, 147.76) * mm});
            skLineSegment(sketch, "E9", {"start": v(-257.76, 147.76) * mm, "end": v(44.24, 147.76) * mm});
            skLineSegment(sketch, "E10", {"start": v(44.24, 147.76) * mm, "end": v(44.24, 117.76) * mm});
            skLineSegment(sketch, "E11", {"start": v(-57.76, -111.24) * mm, "end": v(-87.76, -111.24) * mm});
            skLineSegment(sketch, "E12", {"start": v(-87.76, -111.24) * mm, "end": v(-257.76, 117.76) * mm});
            skPoint(sketch, "E13.0", {"position": v(21.24, 91.76) * mm});
            skPoint(sketch, "E14.0", {"position": v(-31.76, -81.24) * mm});
            skArc(sketch, "E15", {"start": v(33.73, 91.26) * mm, "mid": v(21.24, 104.26) * mm, "end": v(8.75, 91.26) * mm});
            skArc(sketch, "E16", {"start": v(-31.26, -68.75) * mm, "mid": v(-44.26, -81.24) * mm, "end": v(-31.26, -93.73) * mm});
            skPoint(sketch, "E17.0", {"position": v(5.03, 91.26) * mm});
            skLineSegment(sketch, "E18", {"start": v(-26.26, 91.26) * mm, "end": v(8.75, 91.26) * mm});
            skLineSegment(sketch, "E19", {"start": v(33.73, 91.26) * mm, "end": v(44.24, 91.26) * mm});
            skLineSegment(sketch, "E20", {"start": v(44.24, 117.76) * mm, "end": v(44.24, 91.26) * mm});
            skPoint(sketch, "E20.endSnap0", {"position": v(40.56, 91.26) * mm});
            skPoint(sketch, "E21.0", {"position": v(-31.26, -65.03) * mm});
            skLineSegment(sketch, "E22", {"start": v(-31.26, 86.26) * mm, "end": v(-31.26, -68.75) * mm});
            skLineSegment(sketch, "E23", {"start": v(-31.26, -93.73) * mm, "end": v(-31.26, -111.24) * mm});
            skLineSegment(sketch, "E24", {"start": v(-31.26, -111.24) * mm, "end": v(-57.76, -111.24) * mm});
            skPoint(sketch, "E25.visualSharp", {"position": v(-31.26, 91.26) * mm});
            skArc(sketch, "E25.filletArc", {"start": v(-26.26, 91.26) * mm, "mid": v(-29.8, 89.8) * mm, "end": v(-31.26, 86.26) * mm});
            skSolve(sketch);
        }
        {
            var Q0;
            Q0=makeQuery(id+"F1.imprint","IMPRINT",FACE,{"disambiguationData":[TD([[makeQuery(id+"F1.imprint","IMPRINT",EDGE,{"derivedFrom":sQuery(id+"F1.wireOp",EDGE,"E8")}),-1.0]])]});
            extrude(context, id + "F2", {"entities" : qUnion([Q0]), "oppositeDirection" : true, "depth" : 8 * mm});
        }
        {
            var Q0;
            Q0=makeQuery(id+"F2.opExtrude","CAP_FACE",FACE,{"disambiguationData":[OSD([sQuery(id+"F1.wireOp",EDGE,"grLMXVx4-REe1-J2QX-cfpd-KUXPb09amYg0"),sQuery(id+"F1.wireOp",EDGE,"85NA8saS-yWfj-IHzV-5X8E-TiR8B10RwH8I"),sQuery(id+"F1.wireOp",EDGE,"bMNJfA2O-k6jC-7edZ-QRAY-Gd5nJX9gFrdN"),sQuery(id+"F1.wireOp",EDGE,"yQ7rgid8-mmXZ-U7ll-9jDd-nNigDscmGfBs"),sQuery(id+"F1.wireOp",EDGE,"E8"),sQuery(id+"F1.wireOp",EDGE,"E9"),sQuery(id+"F1.wireOp",EDGE,"E10")])],"isStart":true});
            var sketch = newSketch(context, id + "F3", { "sketchPlane" : qUnion([Q0])});
            skPoint(sketch, "E26", {"position": v(-110.26, 132.76) * mm});
            skSolve(sketch);
        }
        {
            var Q0;
            Q0=sQuery(id+"F3.wireOp",VERTEX,"E26");
            var Q1;
            Q1=makeQuery(id+"F2.opExtrude","SWEPT_BODY",BODY,{"disambiguationData":[OSD([sQuery(id+"F1.wireOp",EDGE,"grLMXVx4-REe1-J2QX-cfpd-KUXPb09amYg0"),sQuery(id+"F1.wireOp",EDGE,"85NA8saS-yWfj-IHzV-5X8E-TiR8B10RwH8I"),sQuery(id+"F1.wireOp",EDGE,"bMNJfA2O-k6jC-7edZ-QRAY-Gd5nJX9gFrdN"),sQuery(id+"F1.wireOp",EDGE,"yQ7rgid8-mmXZ-U7ll-9jDd-nNigDscmGfBs"),sQuery(id+"F1.wireOp",EDGE,"E8"),sQuery(id+"F1.wireOp",EDGE,"E9"),sQuery(id+"F1.wireOp",EDGE,"E10")])]});
            hole(context, id + "F4", {"style" : HoleStyle.SIMPLE, "endStyle" : HoleEndStyle.THROUGH, "holeDiameter" : 15 * mm, "isTappedThrough" : true, "tappedDepth" : 21 * mm, "tapClearance" : 3, "startFromSketch" : true, "locations" : qUnion([Q0]), "scope" : qUnion([Q1])});
        }
        {
            var Q0;
            Q0=makeQuery(id+"F2.opExtrude","CAP_FACE",FACE,{"disambiguationData":[OSD([sQuery(id+"F1.wireOp",EDGE,"grLMXVx4-REe1-J2QX-cfpd-KUXPb09amYg0"),sQuery(id+"F1.wireOp",EDGE,"85NA8saS-yWfj-IHzV-5X8E-TiR8B10RwH8I"),sQuery(id+"F1.wireOp",EDGE,"bMNJfA2O-k6jC-7edZ-QRAY-Gd5nJX9gFrdN"),sQuery(id+"F1.wireOp",EDGE,"yQ7rgid8-mmXZ-U7ll-9jDd-nNigDscmGfBs"),sQuery(id+"F1.wireOp",EDGE,"E8"),sQuery(id+"F1.wireOp",EDGE,"E9"),sQuery(id+"F1.wireOp",EDGE,"E10")])],"isStart":true});
            var sketch = newSketch(context, id + "F5", { "sketchPlane" : qUnion([Q0])});
            skPoint(sketch, "E27", {"position": v(-72.76, -96.24) * mm});
            skPoint(sketch, "E28", {"position": v(-72.76, -66.24) * mm});
            skPoint(sketch, "E29", {"position": v(-72.76, 102.76) * mm});
            skPoint(sketch, "E30", {"position": v(-72.76, 132.76) * mm});
            skPoint(sketch, "E31", {"position": v(-35.76, 132.76) * mm});
            skPoint(sketch, "E32", {"position": v(24.24, 132.76) * mm});
            skSolve(sketch);
        }
        {
            var Q0;
            Q0=sQuery(id+"F5.wireOp",VERTEX,"E28");
            var Q1;
            Q1=sQuery(id+"F5.wireOp",VERTEX,"E27");
            var Q2;
            Q2=sQuery(id+"F5.wireOp",VERTEX,"E30");
            var Q3;
            Q3=sQuery(id+"F5.wireOp",VERTEX,"E29");
            var Q4;
            Q4=makeQuery(id+"F2.opExtrude","SWEPT_BODY",BODY,{"disambiguationData":[OSD([sQuery(id+"F1.wireOp",EDGE,"grLMXVx4-REe1-J2QX-cfpd-KUXPb09amYg0"),sQuery(id+"F1.wireOp",EDGE,"85NA8saS-yWfj-IHzV-5X8E-TiR8B10RwH8I"),sQuery(id+"F1.wireOp",EDGE,"bMNJfA2O-k6jC-7edZ-QRAY-Gd5nJX9gFrdN"),sQuery(id+"F1.wireOp",EDGE,"yQ7rgid8-mmXZ-U7ll-9jDd-nNigDscmGfBs"),sQuery(id+"F1.wireOp",EDGE,"E8"),sQuery(id+"F1.wireOp",EDGE,"E9"),sQuery(id+"F1.wireOp",EDGE,"E10")])]});
            hole(context, id + "F6", {"style" : HoleStyle.SIMPLE, "endStyle" : HoleEndStyle.THROUGH, "holeDiameter" : 9 * mm, "isTappedThrough" : true, "tappedDepth" : 21 * mm, "tapClearance" : 3, "startFromSketch" : true, "locations" : qUnion([Q0, Q1, Q2, Q3]), "scope" : qUnion([Q4])});
        }
        {
            var Q0;
            Q0=makeQuery(id+"F2.opExtrude","CAP_FACE",FACE,{"disambiguationData":[OSD([sQuery(id+"F1.wireOp",EDGE,"E8"),sQuery(id+"F1.wireOp",EDGE,"E9"),sQuery(id+"F1.wireOp",EDGE,"E10"),sQuery(id+"F1.wireOp",EDGE,"E11"),sQuery(id+"F1.wireOp",EDGE,"E12"),sQuery(id+"F1.wireOp",EDGE,"E15"),sQuery(id+"F1.wireOp",EDGE,"E16"),sQuery(id+"F1.wireOp",EDGE,"E18"),sQuery(id+"F1.wireOp",EDGE,"E19"),sQuery(id+"F1.wireOp",EDGE,"E20"),sQuery(id+"F1.wireOp",EDGE,"E22"),sQuery(id+"F1.wireOp",EDGE,"E23"),sQuery(id+"F1.wireOp",EDGE,"E24"),sQuery(id+"F1.wireOp",EDGE,"E25.filletArc")])],"isStart":true});
            var sketch = newSketch(context, id + "F7", { "sketchPlane" : qUnion([Q0])});
            skCircle(sketch, "E33.0", {"center": v(-110.26, 132.76) * mm, "radius": 7.5 * mm});
            skArc(sketch, "E34", {"start": v(-209.76, 132.76) * mm, "mid": v(-180.62, 62.4) * mm, "end": v(-110.27, 33.26) * mm});
            skArc(sketch, "E35.0", {"start": v(-217.76, 132.76) * mm, "mid": v(-186.28, 56.75) * mm, "end": v(-110.27, 25.26) * mm});
            skArc(sketch, "E36", {"start": v(-217.76, 132.76) * mm, "mid": v(-213.76, 136.76) * mm, "end": v(-209.76, 132.76) * mm});
            skArc(sketch, "E37", {"start": v(-110.27, 33.26) * mm, "mid": v(-106.27, 29.26) * mm, "end": v(-110.27, 25.26) * mm});
            skSolve(sketch);
        }
        {
            var Q0;
            Q0=makeQuery(id+"F7.imprint","IMPRINT",FACE,{"disambiguationData":[TD([[makeQuery(id+"F7.imprint","IMPRINT",EDGE,{"derivedFrom":sQuery(id+"F7.wireOp",EDGE,"E34")}),-1.0]])]});
            extrude(context, id + "F8", {"entities" : qUnion([Q0]), "operationType" : NewBodyOperationType.REMOVE, "oppositeDirection" : true, "depth" : 25 * mm});
        }
        {
            var Q0;
            Q0=sQuery(id+"F5.wireOp",VERTEX,"E31");
            var Q1;
            Q1=sQuery(id+"F5.wireOp",VERTEX,"E32");
            var Q2;
            Q2=makeQuery(id+"F2.opExtrude","SWEPT_BODY",BODY,{"disambiguationData":[OSD([sQuery(id+"F1.wireOp",EDGE,"E8"),sQuery(id+"F1.wireOp",EDGE,"E9"),sQuery(id+"F1.wireOp",EDGE,"E10"),sQuery(id+"F1.wireOp",EDGE,"E11"),sQuery(id+"F1.wireOp",EDGE,"E12"),sQuery(id+"F1.wireOp",EDGE,"E15"),sQuery(id+"F1.wireOp",EDGE,"E16"),sQuery(id+"F1.wireOp",EDGE,"E18"),sQuery(id+"F1.wireOp",EDGE,"E19"),sQuery(id+"F1.wireOp",EDGE,"E20"),sQuery(id+"F1.wireOp",EDGE,"E22"),sQuery(id+"F1.wireOp",EDGE,"E23"),sQuery(id+"F1.wireOp",EDGE,"E24"),sQuery(id+"F1.wireOp",EDGE,"E25.filletArc")])]});
            hole(context, id + "F9", {"style" : HoleStyle.SIMPLE, "endStyle" : HoleEndStyle.THROUGH, "standardTappedOrClearance" : lookupTablePath({ "standard" : "ISO", "size" : "6", "type" : "Drilled" }), "standardBlindInLast" : lookupTablePath({ "standard" : "ISO", "size" : "6", "type" : "Drilled" }), "holeDiameter" : 6 * mm, "tappedDepth" : 15 * mm, "tapClearance" : 3, "startFromSketch" : true, "locations" : qUnion([Q0, Q1]), "scope" : qUnion([Q2])});
        }
    });
